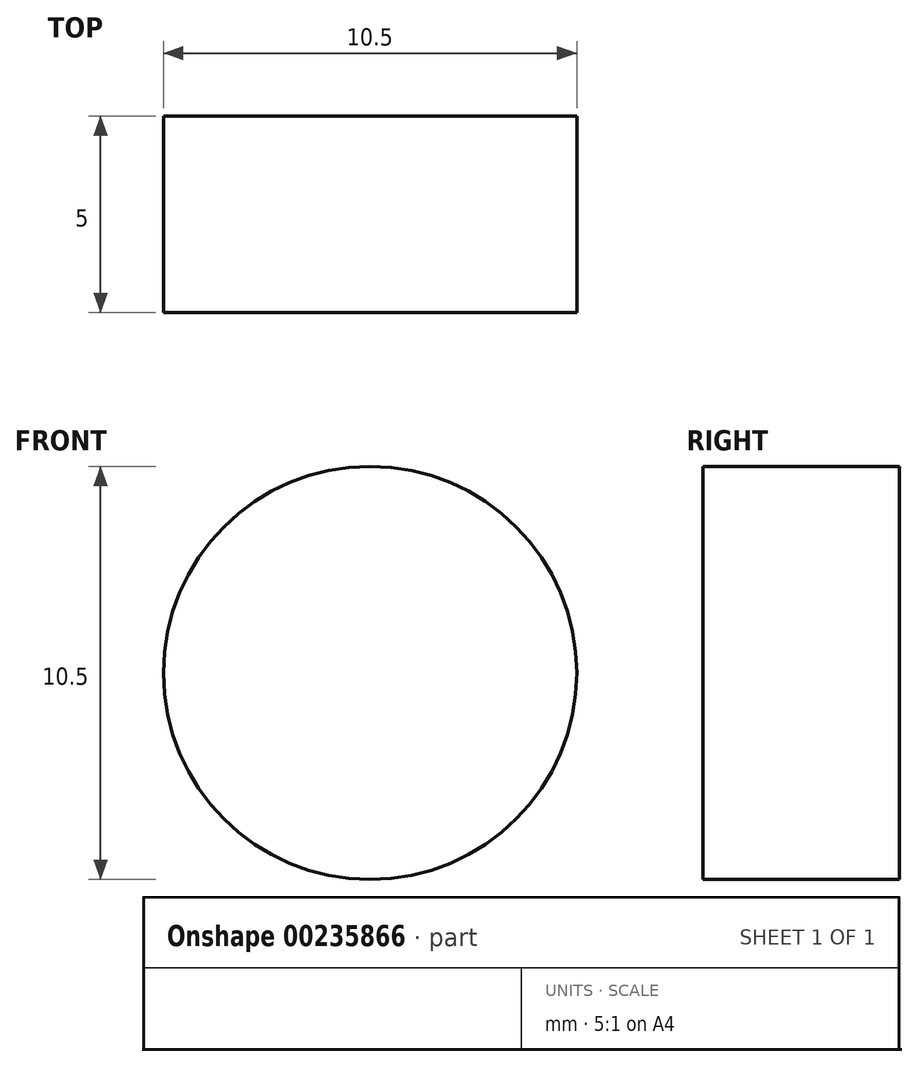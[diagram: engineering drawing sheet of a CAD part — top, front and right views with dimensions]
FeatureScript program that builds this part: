
annotation { "Feature Type Name" : "Feature", "Feature Type Description" : "" }
export const myFeature = defineFeature(function(context is Context, id is Id, definition is map)
    precondition{}
    {
        {
            var Q0;
            Q0=qCreatedBy(makeId("Front.planeOp"),FACE);
            var sketch = newSketch(context, id + "F0", { "sketchPlane" : qUnion([Q0])});
            skCircle(sketch, "E0", {"center": v(0, 0) * mm, "radius": 5.25 * mm});
            skSolve(sketch);
        }
        {
            var Q0;
            Q0=makeQuery(id+"F0.imprint","IMPRINT",FACE,{"disambiguationData":[TD([[makeQuery(id+"F0.imprint","IMPRINT",EDGE,{"derivedFrom":sQuery(id+"F0.wireOp",EDGE,"E0")}),1.0]])]});
            extrude(context, id + "F1", {"entities" : qUnion([Q0]), "depth" : 5 * mm});
        }
    });
